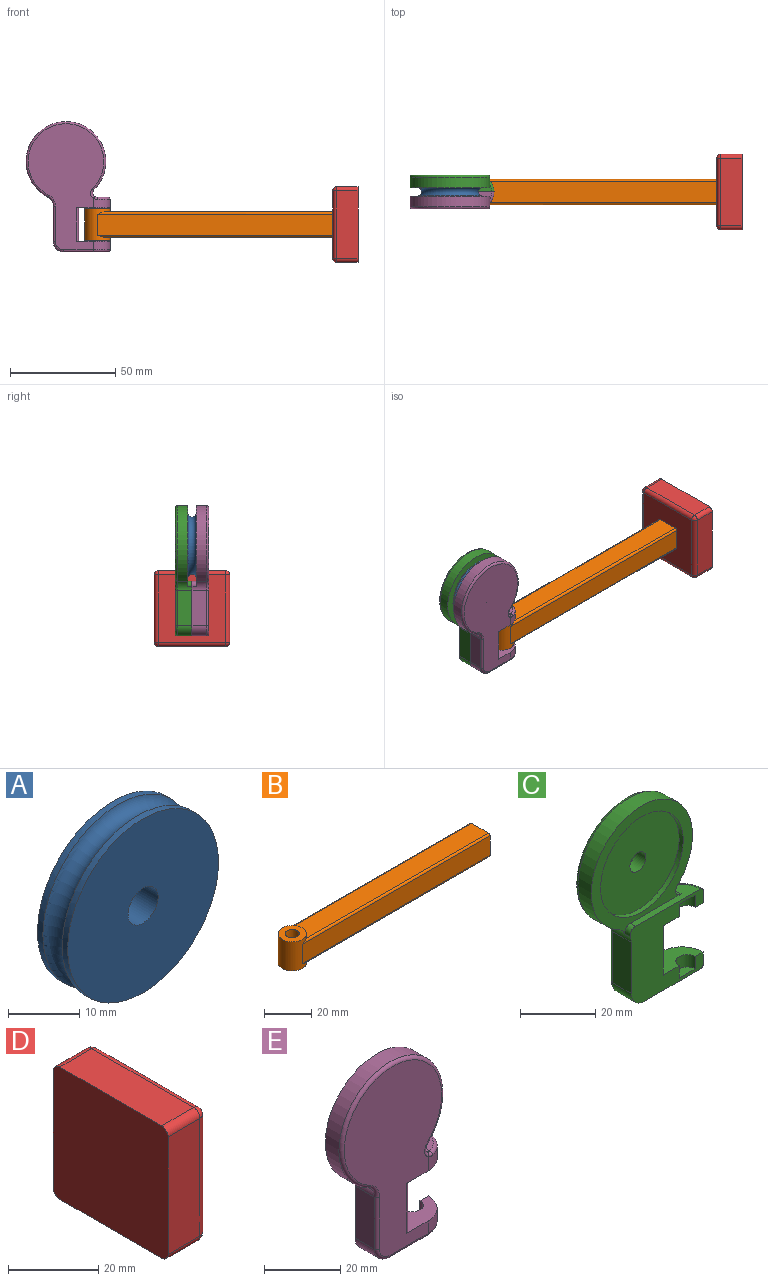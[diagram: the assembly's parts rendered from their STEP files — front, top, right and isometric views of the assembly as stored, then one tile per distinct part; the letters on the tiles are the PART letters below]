
ASSEMBLY  parts=5 mates=4
PART A: 6 faces, bbox 33.6x6x33.6 mm
  f0: cylinder r=15mm len=30mm, axis (0,1,0), area 100.2mm2, adj f4,f5
  f1: cylinder r=15mm len=30mm, axis (0,1,0), area 100.2mm2, adj f3,f5
  f2: cylinder r=3mm len=6mm, axis (0,1,0), area 113.1mm2, adj f3,f4
  f3: plane 30x30mm, normal (0,-1,0), area 678.6mm2, adj f1,f2
  f4: plane 30x30mm, normal (0,1,0), area 678.6mm2, adj f0,f2
  f5: torus R=15.5mm, axis (0,1,0), area 464.8mm2, adj f0,f1
PART B: 13 faces, bbox 118x12x15 mm
  f0: plane 12x12mm, normal (0,0,1), area 84.8mm2, adj f7,f8
  f1: plane 12x12mm, normal (0,0,-1), area 84.8mm2, adj f7,f8
  f2: plane 108.68x10mm, normal (0,0,-1), area 1068mm2, adj f3,f7,f10,f12
  f3: plane 12x12mm, normal (1,0,0), area 143.1mm2, adj f2,f4,f5,f6,f9,f10,f11,f12
  f4: plane 108.68x10mm, normal (0,0,1), area 1068mm2, adj f3,f7,f9,f11
  f5: plane 112x10mm, normal (0,-1,0), area 1120mm2, adj f3,f7,f11,f12
  f6: plane 112x10mm, normal (0,1,0), area 1120mm2, adj f3,f7,f9,f10
  f7: cylinder r=6mm len=15mm, axis (0,0,1), area 344.7mm2, adj f0,f1,f2,f4,f5,f6,f9,f10
  f8: cylinder r=3mm len=15mm, axis (0,0,1), area 282.7mm2, adj f0,f1
  f9: cylinder r=1mm len=112mm, axis (-1,0,0), area 173.1mm2, adj f3,f4,f6,f7
  f10: cylinder r=1mm len=112mm, axis (1,0,0), area 173.1mm2, adj f2,f3,f6,f7
  f11: cylinder r=1mm len=112mm, axis (1,0,0), area 173.1mm2, adj f3,f4,f5,f7
  f12: cylinder r=1mm len=112mm, axis (-1,0,0), area 173.1mm2, adj f2,f3,f5,f7
PART C: 34 faces, bbox 42.2x8.7x64 mm
  f0: plane 27.4x26mm, normal (0,-1,0), area 408.5mm2, adj f3,f4,f5,f6,f7,f8,f9,f10
  f1: cylinder r=2mm len=5mm, axis (0,-1,0), area 23.6mm2, adj f2,f4,f12,f25,f26
  f2: cylinder r=19mm len=38mm, axis (0,-1,0), area 478mm2, adj f1,f5,f12,f27
  f3: plane 16x8mm, normal (0,0,-1), area 92.3mm2, adj f0,f10,f11,f20,f22,f33
  f4: plane 24.4x6.79mm, normal (0,0,1), area 64.9mm2, adj f0,f1,f12,f23,f24
  f5: cylinder r=5mm len=7mm, axis (0,-1,0), area 30.8mm2, adj f0,f2,f6,f12,f23,f28
  f6: plane 16.67x7mm, normal (-1,0,0), area 116.7mm2, adj f0,f5,f7,f29
  f7: cylinder r=5mm len=7mm, axis (0,-1,0), area 55mm2, adj f0,f6,f8,f30
  f8: plane 21x7mm, normal (0,0,-1), area 136.5mm2, adj f0,f7,f31,f32
  f9: plane 16x8mm, normal (0,0,1), area 92.3mm2, adj f0,f10,f11,f17,f21,f33
  f10: plane 16x7mm, normal (1,0,0), area 112mm2, adj f0,f3,f9,f33
  f11: plane 60x36mm, normal (0,1,0), area 1340.1mm2, adj f3,f9,f21,f22,f26,f27,f28,f29
  f12: plane 38.67x38mm, normal (0,-1,0), area 365.7mm2, adj f1,f2,f4,f5,f13,f23
  f13: cylinder r=15.5mm len=31mm, axis (0,-1,0), area 146.1mm2, adj f12,f14
  f14: plane 31x31mm, normal (0,-1,0), area 726.5mm2, adj f13,f15
  f15: cylinder r=3mm len=6mm, axis (0,-1,0), area 75.4mm2, adj f14,f16
  f16: plane 6x6mm, normal (0,-1,0), area 28.3mm2, adj f15
  f17: cylinder r=3mm len=6mm, axis (0,0,-1), area 37.7mm2, adj f0,f9,f18
  f18: plane 6x3mm, normal (0,0,1), area 14.1mm2, adj f0,f17
  f19: plane 6x3mm, normal (0,0,-1), area 14.1mm2, adj f0,f20
  f20: cylinder r=3mm len=6mm, axis (0,0,-1), area 37.7mm2, adj f0,f3,f19
  f21: cylinder r=8mm len=8mm, axis (0,0,-1), area 50.3mm2, adj f0,f9,f11,f32
  f22: cylinder r=8mm len=8mm, axis (0,0,-1), area 50.6mm2, adj f0,f3,f11,f24,f25
  f23: cylinder r=2mm len=2.67mm, axis (0,-1,0), area 7.6mm2, adj f0,f4,f5,f12
  f24: torus R=7mm, axis (0,0,-1), area 15.9mm2, adj f0,f4,f22,f25
  f25: bspline ~3.3x1.68mm, area 2.5mm2, adj f1,f22,f24,f26
  f26: torus R=3mm, axis (0,1,0), area 6.6mm2, adj f1,f11,f25,f27
  f27: torus R=18mm, axis (0,1,0), area 147.3mm2, adj f2,f11,f26,f28
  f28: torus R=6mm, axis (0,1,0), area 9.2mm2, adj f5,f11,f27,f29
  f29: cylinder r=1mm len=16.67mm, axis (0,0,1), area 26.2mm2, adj f6,f11,f28,f30
  f30: torus R=4mm, axis (0,1,0), area 11.4mm2, adj f7,f11,f29,f31
  f31: cylinder r=1mm len=14mm, axis (-1,0,0), area 22mm2, adj f8,f11,f30,f32
  f32: torus R=7mm, axis (0,0,-1), area 18.8mm2, adj f0,f8,f21,f31
  f33: cylinder r=1mm len=16mm, axis (0,0,-1), area 25.1mm2, adj f3,f9,f10,f11
PART D: 18 faces, bbox 12x36x36 mm
  f0: plane 32x10mm, normal (0,0,-1), area 320mm2, adj f1,f7,f9,f14
  f1: cylinder r=2mm len=10mm, axis (-1,0,0), area 31.4mm2, adj f0,f2,f9,f12
  f2: plane 32x10mm, normal (0,1,0), area 320mm2, adj f1,f3,f9,f10
  f3: cylinder r=2mm len=10mm, axis (-1,0,0), area 31.4mm2, adj f2,f4,f9,f11
  f4: plane 32x10mm, normal (0,0,1), area 320mm2, adj f3,f5,f9,f13
  f5: cylinder r=2mm len=10mm, axis (-1,0,0), area 31.4mm2, adj f4,f6,f9,f15
  f6: plane 32x10mm, normal (0,-1,0), area 320mm2, adj f5,f7,f9,f17
  f7: cylinder r=2mm len=10mm, axis (-1,0,0), area 31.4mm2, adj f0,f6,f9,f16
  f8: plane 32x32mm, normal (1,0,0), area 1024mm2, adj f10,f13,f14,f17
  f9: plane 36x36mm, normal (-1,0,0), area 1292.6mm2, adj f0,f1,f2,f3,f4,f5,f6,f7
  f10: cylinder r=2mm len=32mm, axis (0,0,-1), area 100.5mm2, adj f2,f8,f11,f12
  f11: sphere r=2mm, area 6.3mm2, adj f3,f10,f13
  f12: sphere r=2mm, area 6.3mm2, adj f1,f10,f14
  f13: cylinder r=2mm len=32mm, axis (0,1,0), area 100.5mm2, adj f4,f8,f11,f15
  f14: cylinder r=2mm len=32mm, axis (0,-1,0), area 100.5mm2, adj f0,f8,f12,f16
  f15: sphere r=2mm, area 6.3mm2, adj f5,f13,f17
  f16: sphere r=2mm, area 6.3mm2, adj f7,f14,f17
  f17: cylinder r=2mm len=32mm, axis (0,0,1), area 100.5mm2, adj f6,f8,f15,f16
PART E: 34 faces, bbox 42.2x8.7x64 mm
  f0: plane 27.4x26mm, normal (0,1,0), area 408.5mm2, adj f3,f4,f5,f6,f7,f8,f9,f10
  f1: cylinder r=2mm len=5mm, axis (0,1,0), area 23.6mm2, adj f2,f4,f12,f25,f26
  f2: cylinder r=19mm len=38mm, axis (0,1,0), area 478mm2, adj f1,f5,f12,f27
  f3: plane 16x8mm, normal (0,0,-1), area 92.3mm2, adj f0,f10,f11,f20,f22,f33
  f4: plane 24.4x6.79mm, normal (0,0,1), area 64.9mm2, adj f0,f1,f12,f23,f24
  f5: cylinder r=5mm len=7mm, axis (0,1,0), area 30.8mm2, adj f0,f2,f6,f12,f23,f28
  f6: plane 16.67x7mm, normal (-1,0,0), area 116.7mm2, adj f0,f5,f7,f29
  f7: cylinder r=5mm len=7mm, axis (0,1,0), area 55mm2, adj f0,f6,f8,f30
  f8: plane 21x7mm, normal (0,0,-1), area 136.5mm2, adj f0,f7,f31,f32
  f9: plane 16x8mm, normal (0,0,1), area 92.3mm2, adj f0,f10,f11,f17,f21,f33
  f10: plane 16x7mm, normal (1,0,0), area 112mm2, adj f0,f3,f9,f33
  f11: plane 60x36mm, normal (0,-1,0), area 1340.1mm2, adj f3,f9,f21,f22,f26,f27,f28,f29
  f12: plane 38.67x38mm, normal (0,1,0), area 365.7mm2, adj f1,f2,f4,f5,f13,f23
  f13: cylinder r=15.5mm len=31mm, axis (0,1,0), area 146.1mm2, adj f12,f14
  f14: plane 31x31mm, normal (0,1,0), area 726.5mm2, adj f13,f15
  f15: cylinder r=3mm len=6mm, axis (0,1,0), area 75.4mm2, adj f14,f16
  f16: plane 6x6mm, normal (0,1,0), area 28.3mm2, adj f15
  f17: cylinder r=3mm len=6mm, axis (0,0,-1), area 37.7mm2, adj f0,f9,f18
  f18: plane 6x3mm, normal (0,0,1), area 14.1mm2, adj f0,f17
  f19: plane 6x3mm, normal (0,0,-1), area 14.1mm2, adj f0,f20
  f20: cylinder r=3mm len=6mm, axis (0,0,-1), area 37.7mm2, adj f0,f3,f19
  f21: cylinder r=8mm len=8mm, axis (0,0,-1), area 50.3mm2, adj f0,f9,f11,f32
  f22: cylinder r=8mm len=8mm, axis (0,0,-1), area 50.6mm2, adj f0,f3,f11,f24,f25
  f23: cylinder r=2mm len=2.67mm, axis (0,1,0), area 7.6mm2, adj f0,f4,f5,f12
  f24: torus R=7mm, axis (0,0,-1), area 15.9mm2, adj f0,f4,f22,f25
  f25: bspline ~3.3x1.68mm, area 2.5mm2, adj f1,f22,f24,f26
  f26: torus R=3mm, axis (0,-1,0), area 6.6mm2, adj f1,f11,f25,f27
  f27: torus R=18mm, axis (0,-1,0), area 147.3mm2, adj f2,f11,f26,f28
  f28: torus R=6mm, axis (0,-1,0), area 9.2mm2, adj f5,f11,f27,f29
  f29: cylinder r=1mm len=16.67mm, axis (0,0,1), area 26.2mm2, adj f6,f11,f28,f30
  f30: torus R=4mm, axis (0,-1,0), area 11.4mm2, adj f7,f11,f29,f31
  f31: cylinder r=1mm len=14mm, axis (-1,0,0), area 22mm2, adj f8,f11,f30,f32
  f32: torus R=7mm, axis (0,0,-1), area 18.8mm2, adj f0,f8,f21,f31
  f33: cylinder r=1mm len=16mm, axis (0,0,-1), area 25.1mm2, adj f3,f9,f10,f11
PLACE A t=(-127,3,30)mm
PLACE B t=(-112,0,0)mm
PLACE C t=(-127,0,30)mm
PLACE D rot(axis=(0,1,0),180deg) t=(12,0,0)mm
PLACE E t=(-127,0,30)mm
MATE fastened C.f13 <-> A.f2  axis (0,-1,0) through (-127,3.5,30)mm
MATE fastened B.f3 <-> D.f8  axis (1,0,0) through (0,0,0)mm
MATE revolute E.f17 <-> B.f8  axis (0,0,1) through (-112,0,-8)mm
MATE fastened C.f0 <-> E.f0  axis (0,-1,0) through (-121,0,0)mm
